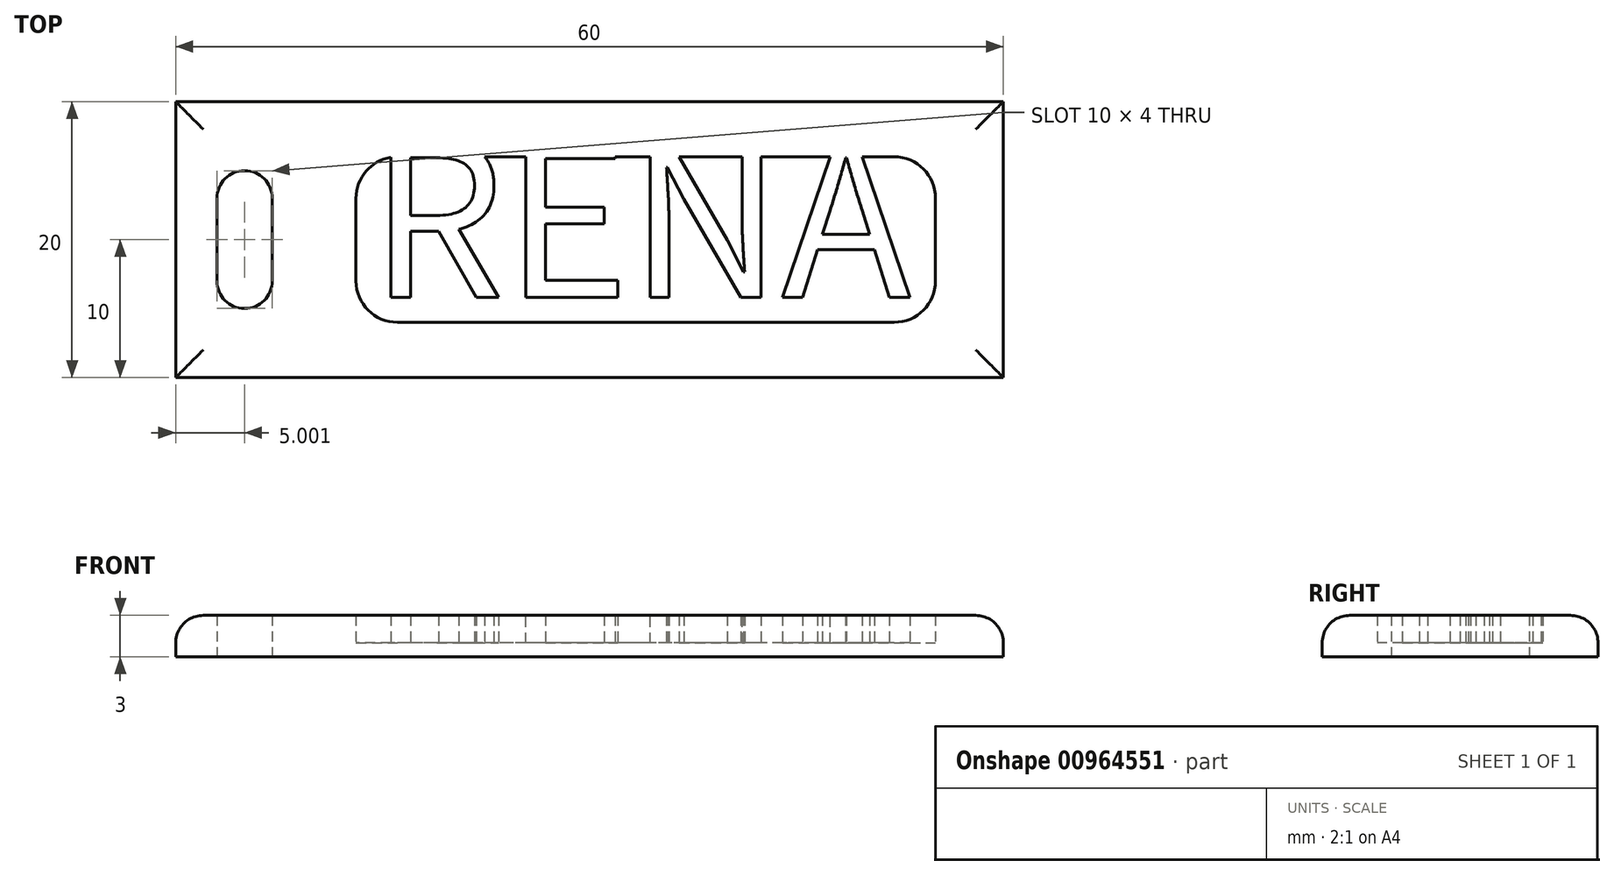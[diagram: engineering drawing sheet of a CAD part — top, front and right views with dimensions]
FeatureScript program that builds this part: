
annotation { "Feature Type Name" : "Feature", "Feature Type Description" : "" }
export const myFeature = defineFeature(function(context is Context, id is Id, definition is map)
    precondition{}
    {
        {
            var Q0;
            Q0=qCreatedBy(makeId("Top.planeOp"),FACE);
            var sketch = newSketch(context, id + "F0", { "sketchPlane" : qUnion([Q0])});
            skLineSegment(sketch, "E0.bottom", {"start": v(25.92, 10) * mm, "end": v(-24.08, 10) * mm});
            skLineSegment(sketch, "E0.top", {"start": v(25.92, -10) * mm, "end": v(-24.08, -10) * mm});
            skLineSegment(sketch, "E0.left", {"start": v(25.92, 10) * mm, "end": v(25.92, -10) * mm});
            skLineSegment(sketch, "E0.right", {"start": v(-24.08, 10) * mm, "end": v(-24.08, -10) * mm});
            skPoint(sketch, "E0.middle", {"position": v(0.92, 0) * mm});
            skLineSegment(sketch, "E1.bottom", {"start": v(-24.08, 10) * mm, "end": v(-34.08, 10) * mm});
            skLineSegment(sketch, "E1.top", {"start": v(-24.08, -10) * mm, "end": v(-34.08, -10) * mm});
            skLineSegment(sketch, "E1.right", {"start": v(-34.08, 10) * mm, "end": v(-34.08, -10) * mm});
            skPoint(sketch, "E1.middle", {"position": v(-29.08, 0) * mm});
            skLineSegment(sketch, "E2.bottom", {"start": v(-29.08, 5) * mm, "end": v(-29.08, 5) * mm});
            skLineSegment(sketch, "E2.top", {"start": v(-29.08, -5) * mm, "end": v(-29.08, -5) * mm});
            skLineSegment(sketch, "E2.left", {"start": v(-31.08, 3) * mm, "end": v(-31.08, -3) * mm});
            skLineSegment(sketch, "E2.right", {"start": v(-27.08, 3) * mm, "end": v(-27.08, -3) * mm});
            skPoint(sketch, "E3.visualSharp", {"position": v(-31.08, 5) * mm});
            skArc(sketch, "E3.filletArc", {"start": v(-29.08, 5) * mm, "mid": v(-30.5, 4.41) * mm, "end": v(-31.08, 3) * mm});
            skPoint(sketch, "E4.visualSharp", {"position": v(-27.08, 5) * mm});
            skArc(sketch, "E4.filletArc", {"start": v(-27.08, 3) * mm, "mid": v(-27.67, 4.41) * mm, "end": v(-29.08, 5) * mm});
            skPoint(sketch, "E5.visualSharp", {"position": v(-31.08, -5) * mm});
            skArc(sketch, "E5.filletArc", {"start": v(-31.08, -3) * mm, "mid": v(-30.5, -4.41) * mm, "end": v(-29.08, -5) * mm});
            skPoint(sketch, "E6.visualSharp", {"position": v(-27.08, -5) * mm});
            skArc(sketch, "E6.filletArc", {"start": v(-29.08, -5) * mm, "mid": v(-27.67, -4.41) * mm, "end": v(-27.08, -3) * mm});
            skSolve(sketch);
        }
        {
            var Q0;
            Q0 = qSketchRegion(id + "F0", true);
            extrude(context, id + "F1", {"entities" : qUnion([Q0]), "depth" : 3 * mm, "offsetDistance" : 25 * mm});
        }
        {
            var Q0;
            Q0=qCreatedBy(makeId("Top.planeOp"),FACE);
            var sketch = newSketch(context, id + "F2", { "sketchPlane" : qUnion([Q0])});
            skLineSegment(sketch, "E7.bottom", {"start": v(18, 6) * mm, "end": v(-18, 6) * mm});
            skLineSegment(sketch, "E7.top", {"start": v(18, -6) * mm, "end": v(-18, -6) * mm});
            skLineSegment(sketch, "E7.left", {"start": v(21, 3) * mm, "end": v(21, -3) * mm});
            skLineSegment(sketch, "E7.right", {"start": v(-21, 3) * mm, "end": v(-21, -3) * mm});
            skPoint(sketch, "E7.middle", {"position": v(0, 0) * mm});
            skPoint(sketch, "E8.visualSharp", {"position": v(-21, 6) * mm});
            skArc(sketch, "E8.filletArc", {"start": v(-18, 6) * mm, "mid": v(-20.12, 5.12) * mm, "end": v(-21, 3) * mm});
            skPoint(sketch, "E9.visualSharp", {"position": v(-21, -6) * mm});
            skArc(sketch, "E9.filletArc", {"start": v(-21, -3) * mm, "mid": v(-20.12, -5.12) * mm, "end": v(-18, -6) * mm});
            skPoint(sketch, "E10.visualSharp", {"position": v(21, 6) * mm});
            skArc(sketch, "E10.filletArc", {"start": v(21, 3) * mm, "mid": v(20.12, 5.12) * mm, "end": v(18, 6) * mm});
            skPoint(sketch, "E11.visualSharp", {"position": v(21, -6) * mm});
            skArc(sketch, "E11.filletArc", {"start": v(18, -6) * mm, "mid": v(20.12, -5.12) * mm, "end": v(21, -3) * mm});
            skSolve(sketch);
        }
        {
            var Q0;
            Q0 = qSketchRegion(id + "F2", true);
            extrude(context, id + "F3", {"entities" : qUnion([Q0]), "depth" : 3 * mm, "offsetDistance" : 25 * mm});
        }
        {
            var Q0;
            Q0=makeQuery(id+"F3.opExtrude","SWEPT_BODY",BODY,{"disambiguationData":[OSD([sQuery(id+"F2.wireOp",EDGE,"E7.bottom"),sQuery(id+"F2.wireOp",EDGE,"E7.top"),sQuery(id+"F2.wireOp",EDGE,"E7.left"),sQuery(id+"F2.wireOp",EDGE,"E7.right"),sQuery(id+"F2.wireOp",EDGE,"E8.filletArc"),sQuery(id+"F2.wireOp",EDGE,"E9.filletArc"),sQuery(id+"F2.wireOp",EDGE,"E10.filletArc"),sQuery(id+"F2.wireOp",EDGE,"E11.filletArc")])]});
            transform(context, id + "F4", {"entities" : qUnion([Q0]), "transformType" : TransformType.TRANSLATION_3D, "dx" : 0 * mm, "dy" : 0 * mm, "dz" : 1 * mm, "makeCopy" : false});
        }
        {
            var Q0;
            Q0=makeQuery(id+"F3.opExtrude","SWEPT_BODY",BODY,{"disambiguationData":[OSD([sQuery(id+"F2.wireOp",EDGE,"E7.bottom"),sQuery(id+"F2.wireOp",EDGE,"E7.top"),sQuery(id+"F2.wireOp",EDGE,"E7.left"),sQuery(id+"F2.wireOp",EDGE,"E7.right"),sQuery(id+"F2.wireOp",EDGE,"E8.filletArc"),sQuery(id+"F2.wireOp",EDGE,"E9.filletArc"),sQuery(id+"F2.wireOp",EDGE,"E10.filletArc"),sQuery(id+"F2.wireOp",EDGE,"E11.filletArc")])]});
            var Q1;
            Q1=makeQuery(id+"F1.opExtrude","SWEPT_BODY",BODY,{"disambiguationData":[OSD([sQuery(id+"F0.wireOp",EDGE,"E0.bottom"),sQuery(id+"F0.wireOp",EDGE,"E0.top"),sQuery(id+"F0.wireOp",EDGE,"E0.left"),sQuery(id+"F0.wireOp",EDGE,"E1.bottom"),sQuery(id+"F0.wireOp",EDGE,"E1.top"),sQuery(id+"F0.wireOp",EDGE,"E1.right"),sQuery(id+"F0.wireOp",EDGE,"E2.left"),sQuery(id+"F0.wireOp",EDGE,"E2.right"),sQuery(id+"F0.wireOp",EDGE,"E3.filletArc"),sQuery(id+"F0.wireOp",EDGE,"E4.filletArc"),sQuery(id+"F0.wireOp",EDGE,"E5.filletArc"),sQuery(id+"F0.wireOp",EDGE,"E6.filletArc")])]});
            booleanBodies(context, id + "F5", {"operationType" : BooleanOperationType.SUBTRACTION, "tools" : qUnion([Q0]), "targets" : qUnion([Q1])});
        }
        {
            var Q0;
            Q0=qCreatedBy(makeId("Top.planeOp"),FACE);
            var sketch = newSketch(context, id + "F6", { "sketchPlane" : qUnion([Q0])});
            skText(sketch, "E12", { "text": "RENA", "fontName": "NotoSansCJKjp-Regular.otf"});
            const initialGuessF6  = {"E12": [-0.02, -0.00418, 1, 0, 0.01106]};
            skSetInitialGuess(sketch, initialGuessF6);
            skSolve(sketch);
        }
        {
            var Q0;
            Q0 = qSketchRegion(id + "F6", true);
            extrude(context, id + "F7", {"entities" : qUnion([Q0]), "operationType" : NewBodyOperationType.ADD, "depth" : 3 * mm, "offsetDistance" : 25 * mm});
        }
        {
            var Q0;
            Q0=makeQuery(id+"F1.opExtrude","CAP_EDGE",EDGE,{"disambiguationData":[OSD([sQuery(id+"F0.wireOp",EDGE,"E1.right")])],"isStart":false});
            var Q1;
            Q1=makeQuery(id+"F1.opExtrude","CAP_EDGE",EDGE,{"disambiguationData":[OSD([sQuery(id+"F0.wireOp",EDGE,"E0.bottom"),sQuery(id+"F0.wireOp",EDGE,"E1.bottom")])],"isStart":false});
            var Q2;
            Q2=makeQuery(id+"F1.opExtrude","CAP_EDGE",EDGE,{"disambiguationData":[OSD([sQuery(id+"F0.wireOp",EDGE,"E0.left")])],"isStart":false});
            var Q3;
            Q3=makeQuery(id+"F1.opExtrude","CAP_EDGE",EDGE,{"disambiguationData":[OSD([sQuery(id+"F0.wireOp",EDGE,"E0.top"),sQuery(id+"F0.wireOp",EDGE,"E1.top")])],"isStart":false});
            fillet(context, id + "F8", {"entities" : qUnion([Q0, Q1, Q2, Q3]), "radius" : 2 * mm, "tangentPropagation" : true, "defaultsChanged" : false, "vertexSettings" : [], "allowEdgeOverflow" : false});
        }
    });
